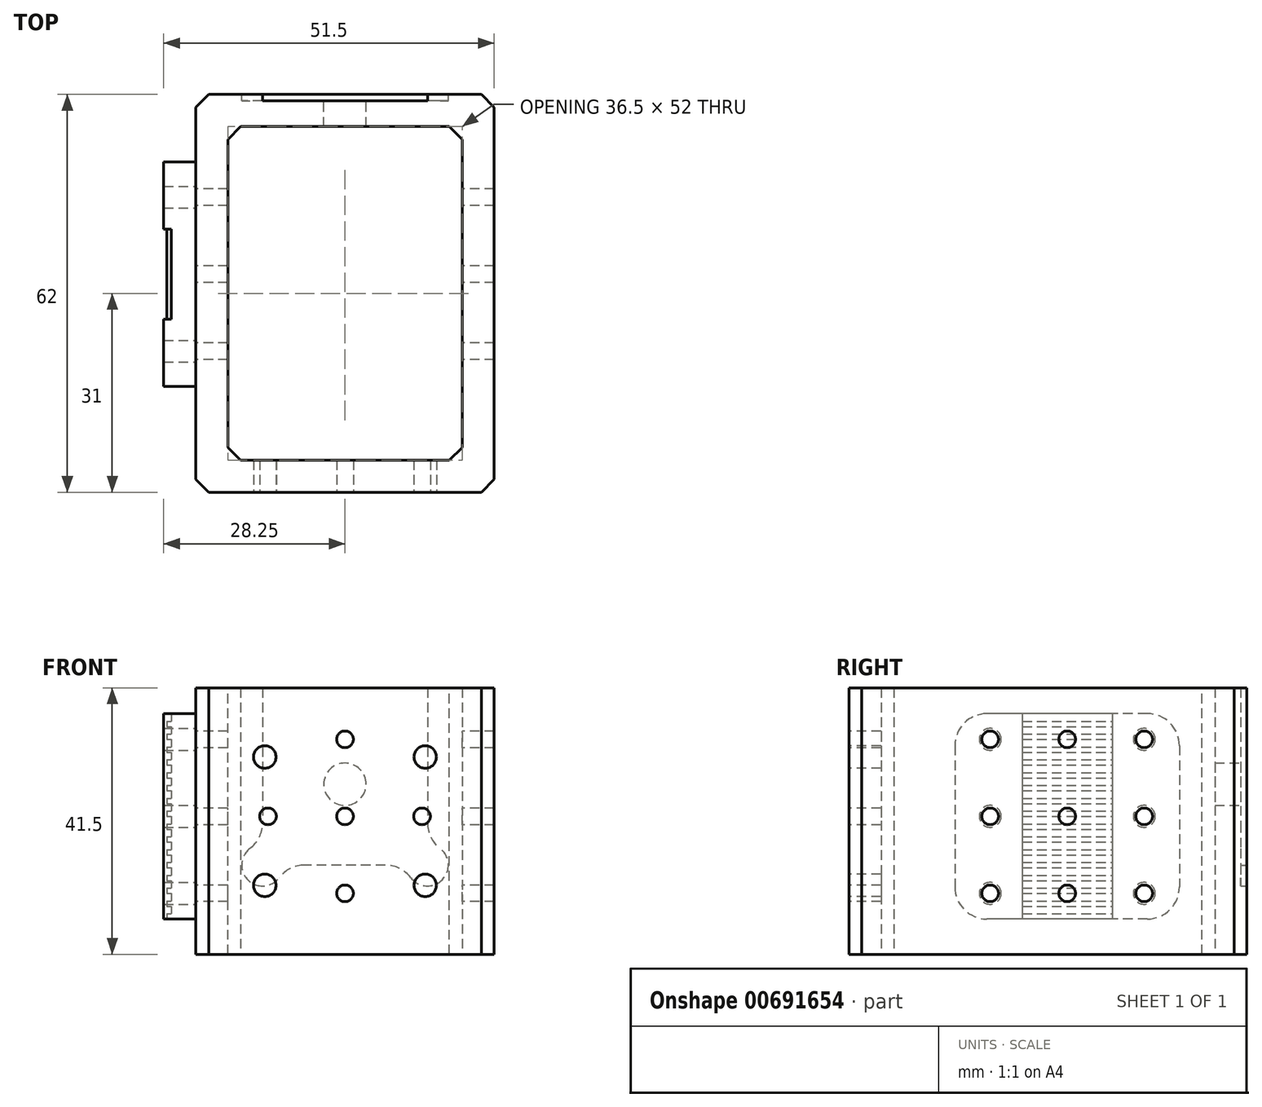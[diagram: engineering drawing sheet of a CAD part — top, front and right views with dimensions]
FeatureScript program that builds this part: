
annotation { "Feature Type Name" : "Feature", "Feature Type Description" : "" }
export const myFeature = defineFeature(function(context is Context, id is Id, definition is map)
    precondition{}
    {
        {
            var Q0;
            Q0=qCreatedBy(makeId("Top.planeOp"),FACE);
            var sketch = newSketch(context, id + "F0", { "sketchPlane" : qUnion([Q0])});
            skLineSegment(sketch, "E0.bottom", {"start": v(-18.25, 26) * mm, "end": v(18.25, 26) * mm});
            skLineSegment(sketch, "E0.top", {"start": v(-18.25, -26) * mm, "end": v(18.25, -26) * mm});
            skLineSegment(sketch, "E0.left", {"start": v(-18.25, 26) * mm, "end": v(-18.25, -26) * mm});
            skLineSegment(sketch, "E0.right", {"start": v(18.25, 26) * mm, "end": v(18.25, -26) * mm});
            skLineSegment(sketch, "E1.0", {"start": v(-23.25, 31) * mm, "end": v(-23.25, -31) * mm});
            skLineSegment(sketch, "E1.1", {"start": v(-23.25, 31) * mm, "end": v(23.25, 31) * mm});
            skLineSegment(sketch, "E1.2", {"start": v(23.25, 31) * mm, "end": v(23.25, -31) * mm});
            skLineSegment(sketch, "E1.3", {"start": v(-23.25, -31) * mm, "end": v(23.25, -31) * mm});
            skSolve(sketch);
        }
        {
            var Q0;
            Q0=qSketchRegion(id+"F0",true);
            extrude(context, id + "F1", {"entities" : qUnion([Q0]), "depth" : 41.5 * mm, "offsetDistance" : 25 * mm});
        }
        {
            var Q0;
            Q0=makeQuery(id+"F1.opExtrude","SWEPT_EDGE",EDGE,{"disambiguationData":[OSD([sQuery(id+"F0.wireOp",EDGE,"E0.bottom"),sQuery(id+"F0.wireOp",EDGE,"E0.right")])]});
            var Q1;
            Q1=makeQuery(id+"F1.opExtrude","SWEPT_EDGE",EDGE,{"disambiguationData":[OSD([sQuery(id+"F0.wireOp",EDGE,"E0.bottom"),sQuery(id+"F0.wireOp",EDGE,"E0.left")])]});
            var Q2;
            Q2=makeQuery(id+"F1.opExtrude","SWEPT_EDGE",EDGE,{"disambiguationData":[OSD([sQuery(id+"F0.wireOp",EDGE,"E0.top"),sQuery(id+"F0.wireOp",EDGE,"E0.right")])]});
            var Q3;
            Q3=makeQuery(id+"F1.opExtrude","SWEPT_EDGE",EDGE,{"disambiguationData":[OSD([sQuery(id+"F0.wireOp",EDGE,"E0.top"),sQuery(id+"F0.wireOp",EDGE,"E0.left")])]});
            var Q4;
            Q4=makeQuery(id+"F1.opExtrude","SWEPT_EDGE",EDGE,{"disambiguationData":[OSD([sQuery(id+"F0.wireOp",EDGE,"E1.0"),sQuery(id+"F0.wireOp",EDGE,"E1.3")])]});
            var Q5;
            Q5=makeQuery(id+"F1.opExtrude","SWEPT_EDGE",EDGE,{"disambiguationData":[OSD([sQuery(id+"F0.wireOp",EDGE,"E1.2"),sQuery(id+"F0.wireOp",EDGE,"E1.3")])]});
            var Q6;
            Q6=makeQuery(id+"F1.opExtrude","SWEPT_EDGE",EDGE,{"disambiguationData":[OSD([sQuery(id+"F0.wireOp",EDGE,"E1.1"),sQuery(id+"F0.wireOp",EDGE,"E1.2")])]});
            var Q7;
            Q7=makeQuery(id+"F1.opExtrude","SWEPT_EDGE",EDGE,{"disambiguationData":[OSD([sQuery(id+"F0.wireOp",EDGE,"E1.0"),sQuery(id+"F0.wireOp",EDGE,"E1.1")])]});
            chamfer(context, id + "F2", {"entities" : qUnion([Q0, Q1, Q2, Q3, Q4, Q5, Q6, Q7]), "width" : 2 * mm, "tangentPropagation" : true});
        }
        {
            var Q0;
            Q0=makeQuery(id+"F1.opExtrude","SWEPT_FACE",FACE,{"disambiguationData":[OSD([sQuery(id+"F0.wireOp",EDGE,"E1.3")])]});
            var sketch = newSketch(context, id + "F3", { "sketchPlane" : qUnion([Q0])});
            skCircle(sketch, "E2", {"center": v(-12.5, 30.75) * mm, "radius": 1.75 * mm});
            skCircle(sketch, "E3", {"center": v(12.5, 30.75) * mm, "radius": 1.75 * mm});
            skCircle(sketch, "E4", {"center": v(-12.5, 10.75) * mm, "radius": 1.75 * mm});
            skCircle(sketch, "E5", {"center": v(12.5, 10.75) * mm, "radius": 1.75 * mm});
            skSolve(sketch);
        }
        {
            var Q0;
            Q0=qSketchRegion(id+"F3",true);
            extrude(context, id + "F4", {"entities" : qUnion([Q0]), "operationType" : NewBodyOperationType.REMOVE, "oppositeDirection" : true, "depth" : 10 * mm, "offsetDistance" : 25 * mm});
        }
        {
            var Q0;
            Q0=makeQuery(id+"F1.opExtrude","SWEPT_FACE",FACE,{"disambiguationData":[OSD([sQuery(id+"F0.wireOp",EDGE,"E1.0")])]});
            var sketch = newSketch(context, id + "F5", { "sketchPlane" : qUnion([Q0])});
            skCircle(sketch, "E6", {"center": v(-3, 33.5) * mm, "radius": 1.3 * mm});
            skCircle(sketch, "E7", {"center": v(-3, 21.5) * mm, "radius": 1.3 * mm});
            skCircle(sketch, "E8", {"center": v(-3, 9.5) * mm, "radius": 1.3 * mm});
            skCircle(sketch, "E9", {"center": v(9, 21.5) * mm, "radius": 1.3 * mm});
            skCircle(sketch, "E10", {"center": v(-15, 21.5) * mm, "radius": 1.3 * mm});
            skCircle(sketch, "E11", {"center": v(-15, 33.5) * mm, "radius": 1.3 * mm});
            skCircle(sketch, "E12", {"center": v(9, 33.5) * mm, "radius": 1.3 * mm});
            skCircle(sketch, "E13", {"center": v(9, 9.5) * mm, "radius": 1.3 * mm});
            skCircle(sketch, "E14", {"center": v(-15, 9.5) * mm, "radius": 1.3 * mm});
            skSolve(sketch);
        }
        {
            var Q0;
            Q0=qSketchRegion(id+"F5",true);
            extrude(context, id + "F6", {"entities" : qUnion([Q0]), "operationType" : NewBodyOperationType.REMOVE, "endBound" : BoundingType.THROUGH_ALL, "oppositeDirection" : true, "depth" : 25 * mm, "offsetDistance" : 25 * mm});
        }
        {
            var Q0;
            Q0=makeQuery(id+"F1.opExtrude","SWEPT_FACE",FACE,{"disambiguationData":[OSD([sQuery(id+"F0.wireOp",EDGE,"E1.1")])]});
            var sketch = newSketch(context, id + "F7", { "sketchPlane" : qUnion([Q0])});
            skCircle(sketch, "E15", {"center": v(0, 26.5) * mm, "radius": 3.3 * mm});
            skSolve(sketch);
        }
        {
            var Q0;
            Q0=qSketchRegion(id+"F7",true);
            extrude(context, id + "F8", {"entities" : qUnion([Q0]), "operationType" : NewBodyOperationType.REMOVE, "oppositeDirection" : true, "depth" : 10 * mm, "offsetDistance" : 25 * mm});
        }
        {
            var Q0;
            Q0=makeQuery(id+"F1.opExtrude","SWEPT_FACE",FACE,{"disambiguationData":[OSD([sQuery(id+"F0.wireOp",EDGE,"E1.1")])]});
            var sketch = newSketch(context, id + "F9", { "sketchPlane" : qUnion([Q0])});
            skLineSegment(sketch, "E16.bottom", {"start": v(-12.85, 41.5) * mm, "end": v(12.85, 41.5) * mm});
            skLineSegment(sketch, "E16.top", {"start": v(-12.85, 13.9) * mm, "end": v(12.85, 13.9) * mm});
            skLineSegment(sketch, "E16.left", {"start": v(-12.85, 41.5) * mm, "end": v(-12.85, 13.9) * mm});
            skLineSegment(sketch, "E16.right", {"start": v(12.85, 41.5) * mm, "end": v(12.85, 13.9) * mm});
            skLineSegment(sketch, "E17", {"start": v(0, 26.5) * mm, "end": v(32.94, 26.5) * mm, "construction": true});
            skSolve(sketch);
        }
        {
            var Q0;
            Q0=qSketchRegion(id+"F9",true);
            extrude(context, id + "F10", {"entities" : qUnion([Q0]), "operationType" : NewBodyOperationType.REMOVE, "oppositeDirection" : true, "depth" : 1 * mm, "offsetDistance" : 25 * mm});
        }
        {
            var Q0;
            Q0=makeQuery(id+"F1.opExtrude","SWEPT_FACE",FACE,{"disambiguationData":[OSD([sQuery(id+"F0.wireOp",EDGE,"E1.1")])]});
            var sketch = newSketch(context, id + "F11", { "sketchPlane" : qUnion([Q0])});
            skCircle(sketch, "E18", {"center": v(-12.85, 13.9) * mm, "radius": 3.25 * mm});
            skCircle(sketch, "E19", {"center": v(12.85, 13.9) * mm, "radius": 3.25 * mm});
            skSolve(sketch);
        }
        {
            var Q0;
            Q0=qSketchRegion(id+"F11",true);
            var Q1;
            Q1=makeQuery(id+"F10.boolean.opBoolean","COPY",FACE,{"derivedFrom":makeQuery(id+"F10.opExtrude","CAP_FACE",FACE,{"disambiguationData":[OSD([sQuery(id+"F9.wireOp",EDGE,"E16.bottom"),sQuery(id+"F9.wireOp",EDGE,"E16.top"),sQuery(id+"F9.wireOp",EDGE,"E16.left"),sQuery(id+"F9.wireOp",EDGE,"E16.right")])],"isStart":false})});
            extrude(context, id + "F12", {"entities" : qUnion([Q0]), "operationType" : NewBodyOperationType.REMOVE, "endBound" : BoundingType.UP_TO_SURFACE, "oppositeDirection" : true, "depth" : 25 * mm, "endBoundEntityFace" : qUnion([Q1]), "offsetDistance" : 25 * mm});
        }
        {
            var Q0;
            Q0=makeQuery(id+"F12.boolean.opBoolean","INTERSECT",EDGE,{"derivedFrom":[makeQuery(id+"F10.boolean.opBoolean","COPY",FACE,{"derivedFrom":makeQuery(id+"F10.opExtrude","SWEPT_FACE",FACE,{"disambiguationData":[OSD([sQuery(id+"F9.wireOp",EDGE,"E16.left")])]})}),makeQuery(id+"F12.opExtrude","SWEPT_FACE",FACE,{"disambiguationData":[OSD([sQuery(id+"F11.wireOp",EDGE,"E18")])]})]});
            var Q1;
            Q1=makeQuery(id+"F12.boolean.opBoolean","INTERSECT",EDGE,{"derivedFrom":[makeQuery(id+"F10.boolean.opBoolean","COPY",FACE,{"derivedFrom":makeQuery(id+"F10.opExtrude","SWEPT_FACE",FACE,{"disambiguationData":[OSD([sQuery(id+"F9.wireOp",EDGE,"E16.right")])]})}),makeQuery(id+"F12.opExtrude","SWEPT_FACE",FACE,{"disambiguationData":[OSD([sQuery(id+"F11.wireOp",EDGE,"E19")])]})]});
            var Q2;
            Q2=makeQuery(id+"F12.boolean.opBoolean","INTERSECT",EDGE,{"derivedFrom":[makeQuery(id+"F10.boolean.opBoolean","COPY",FACE,{"derivedFrom":makeQuery(id+"F10.opExtrude","SWEPT_FACE",FACE,{"disambiguationData":[OSD([sQuery(id+"F9.wireOp",EDGE,"E16.top")])]})}),makeQuery(id+"F12.opExtrude","SWEPT_FACE",FACE,{"disambiguationData":[OSD([sQuery(id+"F11.wireOp",EDGE,"E19")])]})]});
            var Q3;
            Q3=makeQuery(id+"F12.boolean.opBoolean","INTERSECT",EDGE,{"derivedFrom":[makeQuery(id+"F10.boolean.opBoolean","COPY",FACE,{"derivedFrom":makeQuery(id+"F10.opExtrude","SWEPT_FACE",FACE,{"disambiguationData":[OSD([sQuery(id+"F9.wireOp",EDGE,"E16.top")])]})}),makeQuery(id+"F12.opExtrude","SWEPT_FACE",FACE,{"disambiguationData":[OSD([sQuery(id+"F11.wireOp",EDGE,"E18")])]})]});
            fillet(context, id + "F13", {"entities" : qUnion([Q0, Q1, Q2, Q3]), "radius" : 5 * mm, "tangentPropagation" : true, "allowEdgeOverflow" : false});
        }
        {
            var Q0;
            Q0=makeQuery(id+"F1.opExtrude","SWEPT_FACE",FACE,{"disambiguationData":[OSD([sQuery(id+"F0.wireOp",EDGE,"E1.3")])]});
            var sketch = newSketch(context, id + "F14", { "sketchPlane" : qUnion([Q0])});
            skCircle(sketch, "E20", {"center": v(0, 21.5) * mm, "radius": 1.3 * mm});
            skCircle(sketch, "E21", {"center": v(0, 9.5) * mm, "radius": 1.3 * mm});
            skCircle(sketch, "E22", {"center": v(0, 33.5) * mm, "radius": 1.3 * mm});
            skCircle(sketch, "E23", {"center": v(-12, 21.5) * mm, "radius": 1.3 * mm});
            skCircle(sketch, "E24", {"center": v(12, 21.5) * mm, "radius": 1.3 * mm});
            skSolve(sketch);
        }
        {
            var Q0;
            Q0=qSketchRegion(id+"F14",true);
            extrude(context, id + "F15", {"entities" : qUnion([Q0]), "operationType" : NewBodyOperationType.REMOVE, "oppositeDirection" : true, "depth" : 10 * mm, "offsetDistance" : 25 * mm});
        }
        {
            var Q0;
            Q0=makeQuery(id+"F1.opExtrude","SWEPT_FACE",FACE,{"disambiguationData":[OSD([sQuery(id+"F0.wireOp",EDGE,"E1.0")])]});
            var sketch = newSketch(context, id + "F16", { "sketchPlane" : qUnion([Q0])});
            skLineSegment(sketch, "E25.bottom", {"start": v(-15.5, 37.5) * mm, "end": v(9.5, 37.5) * mm});
            skLineSegment(sketch, "E25.top", {"start": v(-15.5, 5.5) * mm, "end": v(9.5, 5.5) * mm});
            skLineSegment(sketch, "E25.left", {"start": v(-20.5, 32.5) * mm, "end": v(-20.5, 10.5) * mm});
            skLineSegment(sketch, "E25.right", {"start": v(14.5, 32.5) * mm, "end": v(14.5, 10.5) * mm});
            skLineSegment(sketch, "E26", {"start": v(-3, 33.5) * mm, "end": v(-3, 9.5) * mm, "construction": true});
            skLineSegment(sketch, "E27", {"start": v(-15, 21.5) * mm, "end": v(9, 21.5) * mm, "construction": true});
            skCircle(sketch, "E28", {"center": v(-15, 21.5) * mm, "radius": 1.7 * mm});
            skCircle(sketch, "E29", {"center": v(9, 21.5) * mm, "radius": 1.7 * mm});
            skCircle(sketch, "E30", {"center": v(-15, 33.5) * mm, "radius": 1.7 * mm});
            skCircle(sketch, "E31", {"center": v(9, 33.5) * mm, "radius": 1.7 * mm});
            skCircle(sketch, "E32", {"center": v(9, 9.5) * mm, "radius": 1.7 * mm});
            skCircle(sketch, "E33", {"center": v(-15, 9.5) * mm, "radius": 1.7 * mm});
            skPoint(sketch, "E34.visualSharp", {"position": v(-20.5, 37.5) * mm});
            skArc(sketch, "E34.filletArc", {"start": v(-15.5, 37.5) * mm, "mid": v(-19.04, 36.04) * mm, "end": v(-20.5, 32.5) * mm});
            skPoint(sketch, "E35.visualSharp", {"position": v(14.5, 37.5) * mm});
            skArc(sketch, "E35.filletArc", {"start": v(14.5, 32.5) * mm, "mid": v(13.04, 36.04) * mm, "end": v(9.5, 37.5) * mm});
            skPoint(sketch, "E36.visualSharp", {"position": v(14.5, 5.5) * mm});
            skArc(sketch, "E36.filletArc", {"start": v(9.5, 5.5) * mm, "mid": v(13.04, 6.96) * mm, "end": v(14.5, 10.5) * mm});
            skPoint(sketch, "E37.visualSharp", {"position": v(-20.5, 5.5) * mm});
            skArc(sketch, "E37.filletArc", {"start": v(-20.5, 10.5) * mm, "mid": v(-19.04, 6.96) * mm, "end": v(-15.5, 5.5) * mm});
            skSolve(sketch);
        }
        {
            var Q0;
            Q0=qSketchRegion(id+"F16",true);
            extrude(context, id + "F17", {"entities" : qUnion([Q0]), "depth" : 5 * mm, "offsetDistance" : 25 * mm});
        }
        {
            var Q0;
            Q0=makeQuery(id+"F17.opExtrude","CAP_FACE",FACE,{"disambiguationData":[OSD([sQuery(id+"F16.wireOp",EDGE,"E25.bottom"),sQuery(id+"F16.wireOp",EDGE,"E25.top"),sQuery(id+"F16.wireOp",EDGE,"E25.left"),sQuery(id+"F16.wireOp",EDGE,"E25.right"),sQuery(id+"F16.wireOp",EDGE,"E28"),sQuery(id+"F16.wireOp",EDGE,"E29"),sQuery(id+"F16.wireOp",EDGE,"E30"),sQuery(id+"F16.wireOp",EDGE,"E31"),sQuery(id+"F16.wireOp",EDGE,"E32"),sQuery(id+"F16.wireOp",EDGE,"E33"),sQuery(id+"F16.wireOp",EDGE,"E34.filletArc"),sQuery(id+"F16.wireOp",EDGE,"E35.filletArc"),sQuery(id+"F16.wireOp",EDGE,"E36.filletArc"),sQuery(id+"F16.wireOp",EDGE,"E37.filletArc")])],"isStart":false});
            var sketch = newSketch(context, id + "F18", { "sketchPlane" : qUnion([Q0])});
            skLineSegment(sketch, "E38.bottom", {"start": v(-10, 37.5) * mm, "end": v(4, 37.5) * mm});
            skLineSegment(sketch, "E38.top", {"start": v(-10, 5.5) * mm, "end": v(4, 5.5) * mm});
            skLineSegment(sketch, "E38.left", {"start": v(-10, 37.5) * mm, "end": v(-10, 5.5) * mm});
            skLineSegment(sketch, "E38.right", {"start": v(4, 37.5) * mm, "end": v(4, 5.5) * mm});
            skLineSegment(sketch, "E39", {"start": v(-15, 21.5) * mm, "end": v(9, 21.5) * mm, "construction": true});
            skLineSegment(sketch, "E40", {"start": v(-3, 21.5) * mm, "end": v(-3, 47.13) * mm, "construction": true});
            skSolve(sketch);
        }
        {
            var Q0;
            Q0=qSketchRegion(id+"F18",true);
            extrude(context, id + "F19", {"entities" : qUnion([Q0]), "operationType" : NewBodyOperationType.REMOVE, "oppositeDirection" : true, "depth" : 1.2 * mm, "offsetDistance" : 25 * mm});
        }
        {
            var Q0;
            Q0=makeQuery(id+"F19.boolean.opBoolean","COPY",FACE,{"derivedFrom":makeQuery(id+"F19.opExtrude","CAP_FACE",FACE,{"disambiguationData":[OSD([sQuery(id+"F18.wireOp",EDGE,"E38.bottom"),sQuery(id+"F18.wireOp",EDGE,"E38.top"),sQuery(id+"F18.wireOp",EDGE,"E38.left"),sQuery(id+"F18.wireOp",EDGE,"E38.right")])],"isStart":false})});
            var sketch = newSketch(context, id + "F20", { "sketchPlane" : qUnion([Q0])});
            skLineSegment(sketch, "E41.bottom", {"start": v(4, 5.5) * mm, "end": v(-10, 5.5) * mm});
            skLineSegment(sketch, "E41.top", {"start": v(4, 6.3) * mm, "end": v(-10, 6.3) * mm});
            skLineSegment(sketch, "E41.left", {"start": v(4, 5.5) * mm, "end": v(4, 6.3) * mm});
            skLineSegment(sketch, "E41.right", {"start": v(-10, 5.5) * mm, "end": v(-10, 6.3) * mm});
            skLineSegment(sketch, "E42.0.1.0", {"start": v(4, 7.5) * mm, "end": v(-10, 7.5) * mm});
            skLineSegment(sketch, "E42.0.1.1", {"start": v(4, 8.3) * mm, "end": v(-10, 8.3) * mm});
            skLineSegment(sketch, "E42.0.1.2", {"start": v(4, 7.5) * mm, "end": v(4, 8.3) * mm});
            skLineSegment(sketch, "E42.0.1.3", {"start": v(-10, 7.5) * mm, "end": v(-10, 8.3) * mm});
            skLineSegment(sketch, "E42.0.2.0", {"start": v(4, 9.5) * mm, "end": v(-10, 9.5) * mm});
            skLineSegment(sketch, "E42.0.2.1", {"start": v(4, 10.3) * mm, "end": v(-10, 10.3) * mm});
            skLineSegment(sketch, "E42.0.2.2", {"start": v(4, 9.5) * mm, "end": v(4, 10.3) * mm});
            skLineSegment(sketch, "E42.0.2.3", {"start": v(-10, 9.5) * mm, "end": v(-10, 10.3) * mm});
            skLineSegment(sketch, "E42.0.3.0", {"start": v(4, 11.5) * mm, "end": v(-10, 11.5) * mm});
            skLineSegment(sketch, "E42.0.3.1", {"start": v(4, 12.3) * mm, "end": v(-10, 12.3) * mm});
            skLineSegment(sketch, "E42.0.3.2", {"start": v(4, 11.5) * mm, "end": v(4, 12.3) * mm});
            skLineSegment(sketch, "E42.0.3.3", {"start": v(-10, 11.5) * mm, "end": v(-10, 12.3) * mm});
            skLineSegment(sketch, "E42.0.4.0", {"start": v(4, 13.5) * mm, "end": v(-10, 13.5) * mm});
            skLineSegment(sketch, "E42.0.4.1", {"start": v(4, 14.3) * mm, "end": v(-10, 14.3) * mm});
            skLineSegment(sketch, "E42.0.4.2", {"start": v(4, 13.5) * mm, "end": v(4, 14.3) * mm});
            skLineSegment(sketch, "E42.0.4.3", {"start": v(-10, 13.5) * mm, "end": v(-10, 14.3) * mm});
            skLineSegment(sketch, "E42.0.5.0", {"start": v(4, 15.5) * mm, "end": v(-10, 15.5) * mm});
            skLineSegment(sketch, "E42.0.5.1", {"start": v(4, 16.3) * mm, "end": v(-10, 16.3) * mm});
            skLineSegment(sketch, "E42.0.5.2", {"start": v(4, 15.5) * mm, "end": v(4, 16.3) * mm});
            skLineSegment(sketch, "E42.0.5.3", {"start": v(-10, 15.5) * mm, "end": v(-10, 16.3) * mm});
            skLineSegment(sketch, "E42.0.6.0", {"start": v(4, 17.5) * mm, "end": v(-10, 17.5) * mm});
            skLineSegment(sketch, "E42.0.6.1", {"start": v(4, 18.3) * mm, "end": v(-10, 18.3) * mm});
            skLineSegment(sketch, "E42.0.6.2", {"start": v(4, 17.5) * mm, "end": v(4, 18.3) * mm});
            skLineSegment(sketch, "E42.0.6.3", {"start": v(-10, 17.5) * mm, "end": v(-10, 18.3) * mm});
            skLineSegment(sketch, "E42.0.7.0", {"start": v(4, 19.5) * mm, "end": v(-10, 19.5) * mm});
            skLineSegment(sketch, "E42.0.7.1", {"start": v(4, 20.3) * mm, "end": v(-10, 20.3) * mm});
            skLineSegment(sketch, "E42.0.7.2", {"start": v(4, 19.5) * mm, "end": v(4, 20.3) * mm});
            skLineSegment(sketch, "E42.0.7.3", {"start": v(-10, 19.5) * mm, "end": v(-10, 20.3) * mm});
            skLineSegment(sketch, "E42.0.8.0", {"start": v(4, 21.5) * mm, "end": v(-10, 21.5) * mm});
            skLineSegment(sketch, "E42.0.8.1", {"start": v(4, 22.3) * mm, "end": v(-10, 22.3) * mm});
            skLineSegment(sketch, "E42.0.8.2", {"start": v(4, 21.5) * mm, "end": v(4, 22.3) * mm});
            skLineSegment(sketch, "E42.0.8.3", {"start": v(-10, 21.5) * mm, "end": v(-10, 22.3) * mm});
            skLineSegment(sketch, "E42.0.9.0", {"start": v(4, 23.5) * mm, "end": v(-10, 23.5) * mm});
            skLineSegment(sketch, "E42.0.9.1", {"start": v(4, 24.3) * mm, "end": v(-10, 24.3) * mm});
            skLineSegment(sketch, "E42.0.9.2", {"start": v(4, 23.5) * mm, "end": v(4, 24.3) * mm});
            skLineSegment(sketch, "E42.0.9.3", {"start": v(-10, 23.5) * mm, "end": v(-10, 24.3) * mm});
            skLineSegment(sketch, "E42.0.10.0", {"start": v(4, 25.5) * mm, "end": v(-10, 25.5) * mm});
            skLineSegment(sketch, "E42.0.10.1", {"start": v(4, 26.3) * mm, "end": v(-10, 26.3) * mm});
            skLineSegment(sketch, "E42.0.10.2", {"start": v(4, 25.5) * mm, "end": v(4, 26.3) * mm});
            skLineSegment(sketch, "E42.0.10.3", {"start": v(-10, 25.5) * mm, "end": v(-10, 26.3) * mm});
            skLineSegment(sketch, "E42.0.11.0", {"start": v(4, 27.5) * mm, "end": v(-10, 27.5) * mm});
            skLineSegment(sketch, "E42.0.11.1", {"start": v(4, 28.3) * mm, "end": v(-10, 28.3) * mm});
            skLineSegment(sketch, "E42.0.11.2", {"start": v(4, 27.5) * mm, "end": v(4, 28.3) * mm});
            skLineSegment(sketch, "E42.0.11.3", {"start": v(-10, 27.5) * mm, "end": v(-10, 28.3) * mm});
            skLineSegment(sketch, "E42.0.12.0", {"start": v(4, 29.5) * mm, "end": v(-10, 29.5) * mm});
            skLineSegment(sketch, "E42.0.12.1", {"start": v(4, 30.3) * mm, "end": v(-10, 30.3) * mm});
            skLineSegment(sketch, "E42.0.12.2", {"start": v(4, 29.5) * mm, "end": v(4, 30.3) * mm});
            skLineSegment(sketch, "E42.0.12.3", {"start": v(-10, 29.5) * mm, "end": v(-10, 30.3) * mm});
            skLineSegment(sketch, "E42.0.13.0", {"start": v(4, 31.5) * mm, "end": v(-10, 31.5) * mm});
            skLineSegment(sketch, "E42.0.13.1", {"start": v(4, 32.3) * mm, "end": v(-10, 32.3) * mm});
            skLineSegment(sketch, "E42.0.13.2", {"start": v(4, 31.5) * mm, "end": v(4, 32.3) * mm});
            skLineSegment(sketch, "E42.0.13.3", {"start": v(-10, 31.5) * mm, "end": v(-10, 32.3) * mm});
            skLineSegment(sketch, "E42.0.14.0", {"start": v(4, 33.5) * mm, "end": v(-10, 33.5) * mm});
            skLineSegment(sketch, "E42.0.14.1", {"start": v(4, 34.3) * mm, "end": v(-10, 34.3) * mm});
            skLineSegment(sketch, "E42.0.14.2", {"start": v(4, 33.5) * mm, "end": v(4, 34.3) * mm});
            skLineSegment(sketch, "E42.0.14.3", {"start": v(-10, 33.5) * mm, "end": v(-10, 34.3) * mm});
            skLineSegment(sketch, "E42.0.15.0", {"start": v(4, 35.5) * mm, "end": v(-10, 35.5) * mm});
            skLineSegment(sketch, "E42.0.15.1", {"start": v(4, 36.3) * mm, "end": v(-10, 36.3) * mm});
            skLineSegment(sketch, "E42.0.15.2", {"start": v(4, 35.5) * mm, "end": v(4, 36.3) * mm});
            skLineSegment(sketch, "E42.0.15.3", {"start": v(-10, 35.5) * mm, "end": v(-10, 36.3) * mm});
            skLineSegment(sketch, "E42.direction1", {"start": v(-10, 5.5) * mm, "end": v(15, 5.5) * mm, "construction": true});
            skLineSegment(sketch, "E42.direction2", {"start": v(-10, 5.5) * mm, "end": v(-10, 7.5) * mm, "construction": true});
            skSolve(sketch);
        }
        {
            var Q0;
            Q0=qSketchRegion(id+"F20",true);
            extrude(context, id + "F21", {"entities" : qUnion([Q0]), "operationType" : NewBodyOperationType.ADD, "depth" : .7 * mm, "offsetDistance" : 25 * mm});
        }
    });
